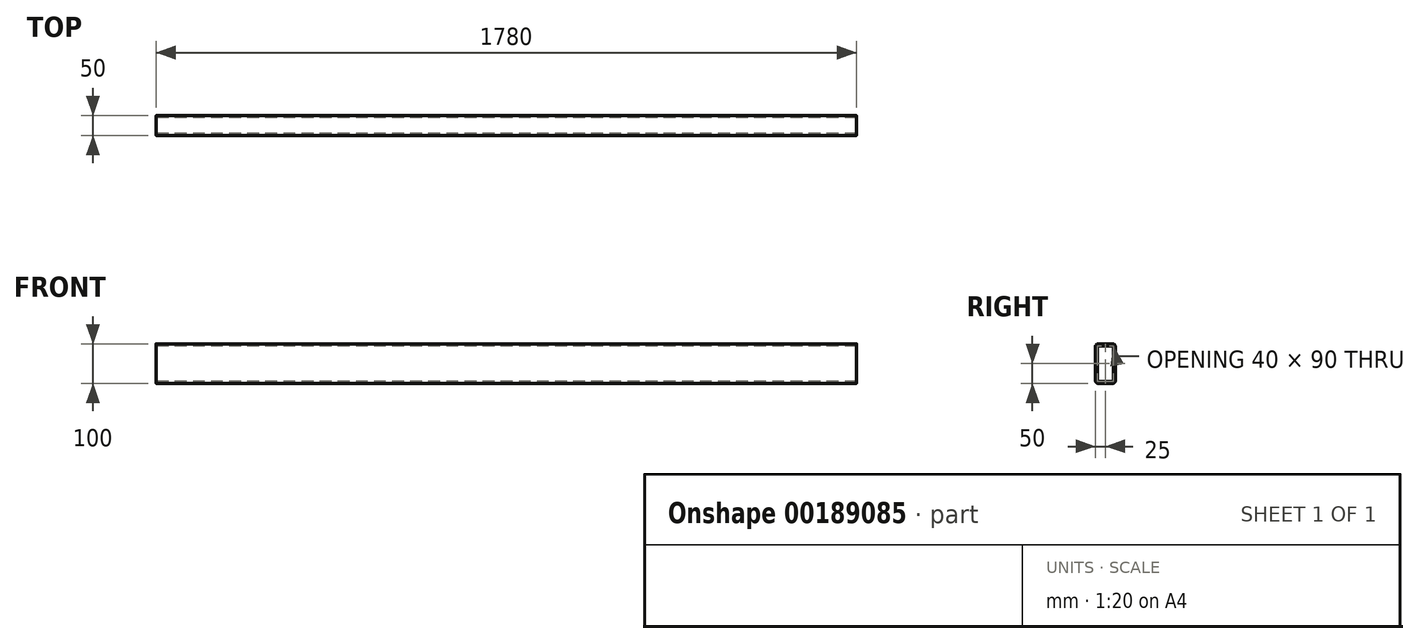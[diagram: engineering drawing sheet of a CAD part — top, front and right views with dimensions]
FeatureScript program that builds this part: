
annotation { "Feature Type Name" : "Feature", "Feature Type Description" : "" }
export const myFeature = defineFeature(function(context is Context, id is Id, definition is map)
    precondition{}
    {
        {
            var Q0;
            Q0=qCreatedBy(makeId("Right.planeOp"),FACE);
            var sketch = newSketch(context, id + "F0", { "sketchPlane" : qUnion([Q0])});
            skLineSegment(sketch, "E0.bottom", {"start": v(25, 50) * mm, "end": v(-25, 50) * mm});
            skLineSegment(sketch, "E0.top", {"start": v(25, -50) * mm, "end": v(-25, -50) * mm});
            skLineSegment(sketch, "E0.left", {"start": v(25, 50) * mm, "end": v(25, -50) * mm});
            skLineSegment(sketch, "E0.right", {"start": v(-25, 50) * mm, "end": v(-25, -50) * mm});
            skPoint(sketch, "E0.middle", {"position": v(0, 0) * mm});
            skLineSegment(sketch, "E1.0", {"start": v(20, 45) * mm, "end": v(-20, 45) * mm});
            skLineSegment(sketch, "E1.1", {"start": v(20, 45) * mm, "end": v(20, -45) * mm});
            skLineSegment(sketch, "E1.2", {"start": v(20, -45) * mm, "end": v(-20, -45) * mm});
            skLineSegment(sketch, "E1.3", {"start": v(-20, 45) * mm, "end": v(-20, -45) * mm});
            skSolve(sketch);
        }
        {
            var Q0;
            Q0=makeQuery(id+"F0.imprint","IMPRINT",FACE,{"disambiguationData":[TD([[makeQuery(id+"F0.imprint","IMPRINT",EDGE,{"derivedFrom":sQuery(id+"F0.wireOp",EDGE,"E0.bottom")}),1.0]])]});
            extrude(context, id + "F1", {"entities" : qUnion([Q0]), "endBound" : BoundingType.SYMMETRIC, "depth" : 1780 * mm});
        }
        {
            var Q0;
            Q0=makeQuery(id+"F1.opExtrude","SWEPT_EDGE",EDGE,{"disambiguationData":[OSD([sQuery(id+"F0.wireOp",EDGE,"E1.0"),sQuery(id+"F0.wireOp",EDGE,"E1.1")])]});
            var Q1;
            Q1=makeQuery(id+"F1.opExtrude","SWEPT_EDGE",EDGE,{"disambiguationData":[OSD([sQuery(id+"F0.wireOp",EDGE,"E1.1"),sQuery(id+"F0.wireOp",EDGE,"E1.2")])]});
            var Q2;
            Q2=makeQuery(id+"F1.opExtrude","SWEPT_EDGE",EDGE,{"disambiguationData":[OSD([sQuery(id+"F0.wireOp",EDGE,"E1.2"),sQuery(id+"F0.wireOp",EDGE,"E1.3")])]});
            var Q3;
            Q3=makeQuery(id+"F1.opExtrude","SWEPT_EDGE",EDGE,{"disambiguationData":[OSD([sQuery(id+"F0.wireOp",EDGE,"E1.0"),sQuery(id+"F0.wireOp",EDGE,"E1.3")])]});
            fillet(context, id + "F2", {"entities" : qUnion([Q0, Q1, Q2, Q3]), "radius" : 3 * mm, "tangentPropagation" : true, "allowEdgeOverflow" : false});
        }
        {
            var Q0;
            Q0=makeQuery(id+"F1.opExtrude","SWEPT_EDGE",EDGE,{"disambiguationData":[OSD([sQuery(id+"F0.wireOp",EDGE,"E0.top"),sQuery(id+"F0.wireOp",EDGE,"E0.left")])]});
            var Q1;
            Q1=makeQuery(id+"F1.opExtrude","SWEPT_EDGE",EDGE,{"disambiguationData":[OSD([sQuery(id+"F0.wireOp",EDGE,"E0.bottom"),sQuery(id+"F0.wireOp",EDGE,"E0.left")])]});
            var Q2;
            Q2=makeQuery(id+"F1.opExtrude","SWEPT_EDGE",EDGE,{"disambiguationData":[OSD([sQuery(id+"F0.wireOp",EDGE,"E0.bottom"),sQuery(id+"F0.wireOp",EDGE,"E0.right")])]});
            var Q3;
            Q3=makeQuery(id+"F1.opExtrude","SWEPT_EDGE",EDGE,{"disambiguationData":[OSD([sQuery(id+"F0.wireOp",EDGE,"E0.top"),sQuery(id+"F0.wireOp",EDGE,"E0.right")])]});
            fillet(context, id + "F3", {"entities" : qUnion([Q0, Q1, Q2, Q3]), "radius" : 6 * mm, "tangentPropagation" : true, "allowEdgeOverflow" : false});
        }
    });
